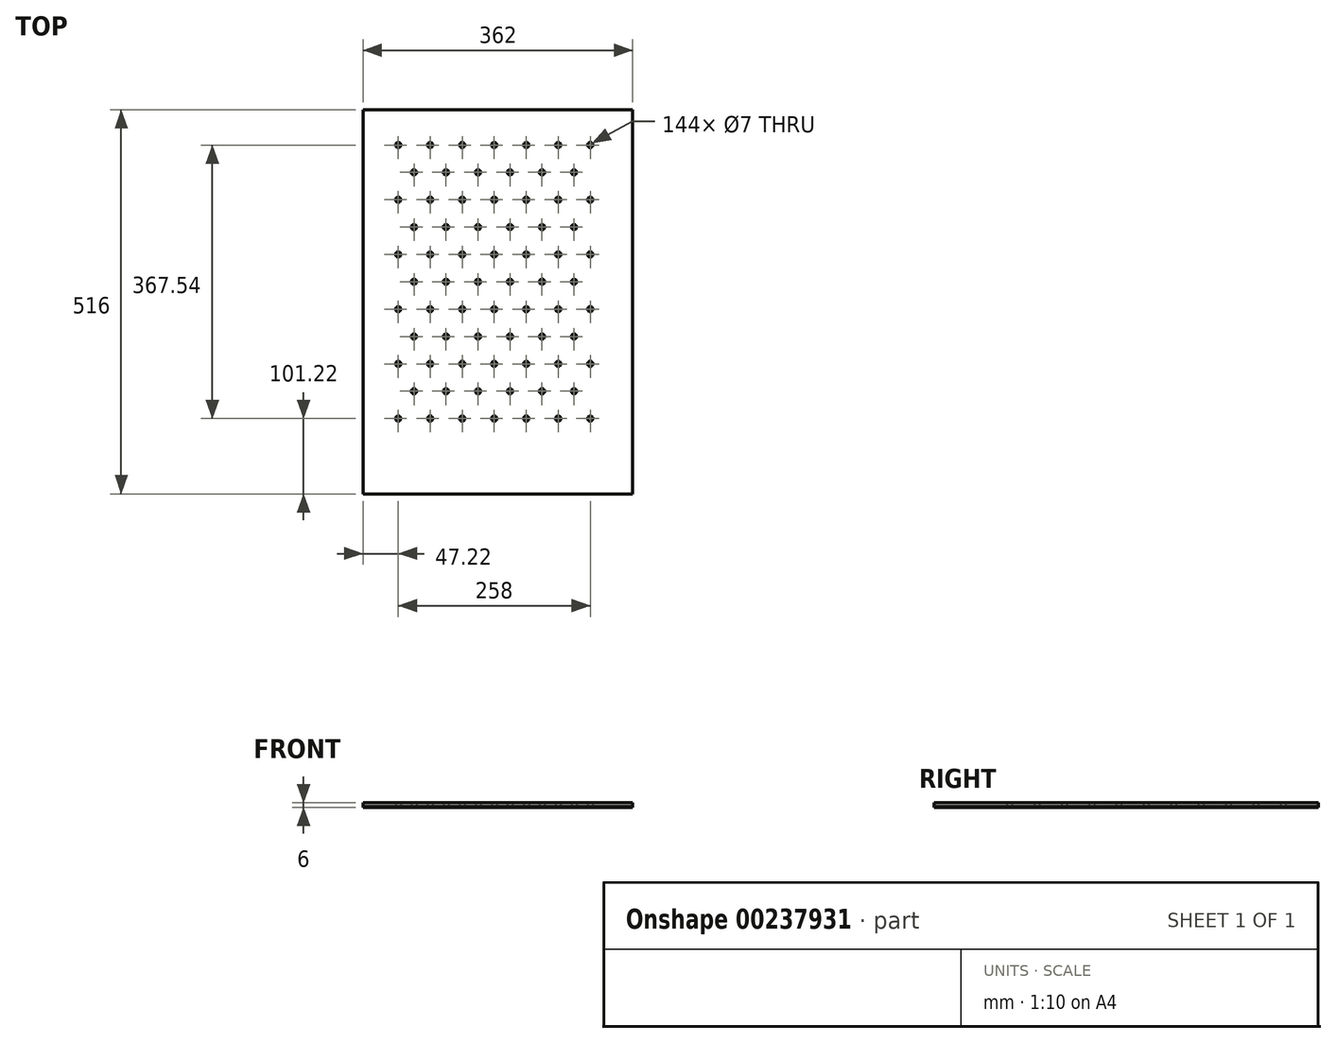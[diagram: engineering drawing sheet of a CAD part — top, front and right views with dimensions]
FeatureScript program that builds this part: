
annotation { "Feature Type Name" : "Feature", "Feature Type Description" : "" }
export const myFeature = defineFeature(function(context is Context, id is Id, definition is map)
    precondition{}
    {
        {
            var Q0;
            Q0=qCreatedBy(makeId("Top.planeOp"),FACE);
            var sketch = newSketch(context, id + "F0", { "sketchPlane" : qUnion([Q0]), "disableImprinting" : false});
            skCircle(sketch, "E0", {"center": v(0, 0) * mm, "radius": 21.22 * mm, "construction": true});
            skLineSegment(sketch, "E1", {"start": v(-21.22, 59.88) * mm, "end": v(-21.22, -39.27) * mm, "construction": true});
            skLineSegment(sketch, "E2", {"start": v(-42.71, -21.22) * mm, "end": v(49.2, -21.22) * mm, "construction": true});
            skLineSegment(sketch, "E3.direction1", {"start": v(0, 0) * mm, "end": v(42.44, 0) * mm, "construction": true});
            skLineSegment(sketch, "E3.direction2", {"start": v(0, -297.48) * mm, "end": v(0, 0) * mm, "construction": true});
            skCircle(sketch, "E4", {"center": v(0, 0) * mm, "radius": 3.5 * mm});
            skCircle(sketch, "E5.0.1.0", {"center": v(0, 73.5) * mm, "radius": 3.5 * mm});
            skCircle(sketch, "E5.0.2.0", {"center": v(0, 147.02) * mm, "radius": 3.5 * mm});
            skCircle(sketch, "E5.0.3.0", {"center": v(0, 220.52) * mm, "radius": 3.5 * mm});
            skCircle(sketch, "E5.0.4.0", {"center": v(0, 294.03) * mm, "radius": 3.5 * mm});
            skCircle(sketch, "E5.0.5.0", {"center": v(0, 367.54) * mm, "radius": 3.5 * mm});
            skCircle(sketch, "E5.1.0.0", {"center": v(43, 0) * mm, "radius": 3.5 * mm});
            skCircle(sketch, "E5.1.1.0", {"center": v(43, 73.5) * mm, "radius": 3.5 * mm});
            skCircle(sketch, "E5.1.2.0", {"center": v(43, 147.02) * mm, "radius": 3.5 * mm});
            skCircle(sketch, "E5.1.3.0", {"center": v(43, 220.52) * mm, "radius": 3.5 * mm});
            skCircle(sketch, "E5.1.4.0", {"center": v(43, 294.03) * mm, "radius": 3.5 * mm});
            skCircle(sketch, "E5.1.5.0", {"center": v(43, 367.54) * mm, "radius": 3.5 * mm});
            skCircle(sketch, "E5.2.0.0", {"center": v(86, 0) * mm, "radius": 3.5 * mm});
            skCircle(sketch, "E5.2.1.0", {"center": v(86, 73.5) * mm, "radius": 3.5 * mm});
            skCircle(sketch, "E5.2.2.0", {"center": v(86, 147.02) * mm, "radius": 3.5 * mm});
            skCircle(sketch, "E5.2.3.0", {"center": v(86, 220.52) * mm, "radius": 3.5 * mm});
            skCircle(sketch, "E5.2.4.0", {"center": v(86, 294.03) * mm, "radius": 3.5 * mm});
            skCircle(sketch, "E5.2.5.0", {"center": v(86, 367.54) * mm, "radius": 3.5 * mm});
            skCircle(sketch, "E5.3.0.0", {"center": v(129, 0) * mm, "radius": 3.5 * mm});
            skCircle(sketch, "E5.3.1.0", {"center": v(129, 73.5) * mm, "radius": 3.5 * mm});
            skCircle(sketch, "E5.3.2.0", {"center": v(129, 147.02) * mm, "radius": 3.5 * mm});
            skCircle(sketch, "E5.3.3.0", {"center": v(129, 220.52) * mm, "radius": 3.5 * mm});
            skCircle(sketch, "E5.3.4.0", {"center": v(129, 294.03) * mm, "radius": 3.5 * mm});
            skCircle(sketch, "E5.3.5.0", {"center": v(129, 367.54) * mm, "radius": 3.5 * mm});
            skCircle(sketch, "E5.4.0.0", {"center": v(172, 0) * mm, "radius": 3.5 * mm});
            skCircle(sketch, "E5.4.1.0", {"center": v(172, 73.5) * mm, "radius": 3.5 * mm});
            skCircle(sketch, "E5.4.2.0", {"center": v(172, 147.02) * mm, "radius": 3.5 * mm});
            skCircle(sketch, "E5.4.3.0", {"center": v(172, 220.52) * mm, "radius": 3.5 * mm});
            skCircle(sketch, "E5.4.4.0", {"center": v(172, 294.03) * mm, "radius": 3.5 * mm});
            skCircle(sketch, "E5.4.5.0", {"center": v(172, 367.54) * mm, "radius": 3.5 * mm});
            skCircle(sketch, "E5.5.0.0", {"center": v(215, 0) * mm, "radius": 3.5 * mm});
            skCircle(sketch, "E5.5.1.0", {"center": v(215, 73.5) * mm, "radius": 3.5 * mm});
            skCircle(sketch, "E5.5.2.0", {"center": v(215, 147.02) * mm, "radius": 3.5 * mm});
            skCircle(sketch, "E5.5.3.0", {"center": v(215, 220.52) * mm, "radius": 3.5 * mm});
            skCircle(sketch, "E5.5.4.0", {"center": v(215, 294.03) * mm, "radius": 3.5 * mm});
            skCircle(sketch, "E5.5.5.0", {"center": v(215, 367.54) * mm, "radius": 3.5 * mm});
            skCircle(sketch, "E5.6.0.0", {"center": v(258, 0) * mm, "radius": 3.5 * mm});
            skCircle(sketch, "E5.6.1.0", {"center": v(258, 73.5) * mm, "radius": 3.5 * mm});
            skCircle(sketch, "E5.6.2.0", {"center": v(258, 147.02) * mm, "radius": 3.5 * mm});
            skCircle(sketch, "E5.6.3.0", {"center": v(258, 220.52) * mm, "radius": 3.5 * mm});
            skCircle(sketch, "E5.6.4.0", {"center": v(258, 294.03) * mm, "radius": 3.5 * mm});
            skCircle(sketch, "E5.6.5.0", {"center": v(258, 367.54) * mm, "radius": 3.5 * mm});
            skLineSegment(sketch, "E5.direction1", {"start": v(0, 0) * mm, "end": v(43, 0) * mm, "construction": true});
            skLineSegment(sketch, "E5.direction2", {"start": v(0, 0) * mm, "end": v(0, 73.5) * mm, "construction": true});
            skLineSegment(sketch, "E6", {"start": v(-21.22, -21.22) * mm, "end": v(288.78, -21.22) * mm, "construction": true});
            skPoint(sketch, "E6.endSnap0", {"position": v(3.24, -21.22) * mm});
            skLineSegment(sketch, "E7", {"start": v(288.78, -21.22) * mm, "end": v(288.78, 388.78) * mm, "construction": true});
            skLineSegment(sketch, "E8", {"start": v(288.78, 388.78) * mm, "end": v(-21.22, 388.78) * mm, "construction": true});
            skLineSegment(sketch, "E9", {"start": v(-21.22, 388.78) * mm, "end": v(-21.22, -21.22) * mm, "construction": true});
            skLineSegment(sketch, "E10", {"start": v(-37.22, 404.78) * mm, "end": v(304.78, 404.78) * mm});
            skLineSegment(sketch, "E11", {"start": v(304.78, 404.78) * mm, "end": v(304.78, -91.22) * mm});
            skLineSegment(sketch, "E12", {"start": v(304.78, -91.22) * mm, "end": v(-37.22, -91.22) * mm});
            skLineSegment(sketch, "E13", {"start": v(-37.22, -91.22) * mm, "end": v(-37.22, 404.78) * mm});
            skCircle(sketch, "E14", {"center": v(42.44, 0) * mm, "radius": 21.22 * mm, "construction": true});
            skCircle(sketch, "E15", {"center": v(21.22, 36.75) * mm, "radius": 21.22 * mm, "construction": true});
            skCircle(sketch, "E16", {"center": v(0, 73.5) * mm, "radius": 21.22 * mm, "construction": true});
            skCircle(sketch, "E17", {"center": v(21.22, 36.75) * mm, "radius": 3.5 * mm});
            skCircle(sketch, "E18.0.1.0", {"center": v(21.22, 110.26) * mm, "radius": 3.5 * mm});
            skCircle(sketch, "E18.0.2.0", {"center": v(21.22, 183.77) * mm, "radius": 3.5 * mm});
            skCircle(sketch, "E18.0.3.0", {"center": v(21.22, 257.28) * mm, "radius": 3.5 * mm});
            skCircle(sketch, "E18.0.4.0", {"center": v(21.22, 330.79) * mm, "radius": 3.5 * mm});
            skCircle(sketch, "E18.1.0.0", {"center": v(64.22, 36.75) * mm, "radius": 3.5 * mm});
            skCircle(sketch, "E18.1.1.0", {"center": v(64.22, 110.26) * mm, "radius": 3.5 * mm});
            skCircle(sketch, "E18.1.2.0", {"center": v(64.22, 183.77) * mm, "radius": 3.5 * mm});
            skCircle(sketch, "E18.1.3.0", {"center": v(64.22, 257.28) * mm, "radius": 3.5 * mm});
            skCircle(sketch, "E18.1.4.0", {"center": v(64.22, 330.79) * mm, "radius": 3.5 * mm});
            skCircle(sketch, "E18.2.0.0", {"center": v(107.22, 36.75) * mm, "radius": 3.5 * mm});
            skCircle(sketch, "E18.2.1.0", {"center": v(107.22, 110.26) * mm, "radius": 3.5 * mm});
            skCircle(sketch, "E18.2.2.0", {"center": v(107.22, 183.77) * mm, "radius": 3.5 * mm});
            skCircle(sketch, "E18.2.3.0", {"center": v(107.22, 257.28) * mm, "radius": 3.5 * mm});
            skCircle(sketch, "E18.2.4.0", {"center": v(107.22, 330.79) * mm, "radius": 3.5 * mm});
            skCircle(sketch, "E18.3.0.0", {"center": v(150.22, 36.75) * mm, "radius": 3.5 * mm});
            skCircle(sketch, "E18.3.1.0", {"center": v(150.22, 110.26) * mm, "radius": 3.5 * mm});
            skCircle(sketch, "E18.3.2.0", {"center": v(150.22, 183.77) * mm, "radius": 3.5 * mm});
            skCircle(sketch, "E18.3.3.0", {"center": v(150.22, 257.28) * mm, "radius": 3.5 * mm});
            skCircle(sketch, "E18.3.4.0", {"center": v(150.22, 330.79) * mm, "radius": 3.5 * mm});
            skCircle(sketch, "E18.4.0.0", {"center": v(193.22, 36.75) * mm, "radius": 3.5 * mm});
            skCircle(sketch, "E18.4.1.0", {"center": v(193.22, 110.26) * mm, "radius": 3.5 * mm});
            skCircle(sketch, "E18.4.2.0", {"center": v(193.22, 183.77) * mm, "radius": 3.5 * mm});
            skCircle(sketch, "E18.4.3.0", {"center": v(193.22, 257.28) * mm, "radius": 3.5 * mm});
            skCircle(sketch, "E18.4.4.0", {"center": v(193.22, 330.79) * mm, "radius": 3.5 * mm});
            skCircle(sketch, "E18.5.0.0", {"center": v(236.22, 36.75) * mm, "radius": 3.5 * mm});
            skCircle(sketch, "E18.5.1.0", {"center": v(236.22, 110.26) * mm, "radius": 3.5 * mm});
            skCircle(sketch, "E18.5.2.0", {"center": v(236.22, 183.77) * mm, "radius": 3.5 * mm});
            skCircle(sketch, "E18.5.3.0", {"center": v(236.22, 257.28) * mm, "radius": 3.5 * mm});
            skCircle(sketch, "E18.5.4.0", {"center": v(236.22, 330.79) * mm, "radius": 3.5 * mm});
            skLineSegment(sketch, "E18.direction1", {"start": v(21.22, 36.75) * mm, "end": v(64.22, 36.75) * mm, "construction": true});
            skLineSegment(sketch, "E18.direction2", {"start": v(21.22, 36.75) * mm, "end": v(21.22, 110.26) * mm, "construction": true});
            skCircle(sketch, "E19", {"center": v(85.72, 171.68) * mm, "radius": 21.17 * mm, "construction": true});
            skLineSegment(sketch, "E20.bottom", {"start": v(80.72, 181.68) * mm, "end": v(90.72, 181.68) * mm, "construction": true});
            skLineSegment(sketch, "E20.top", {"start": v(80.72, 161.68) * mm, "end": v(90.72, 161.68) * mm, "construction": true});
            skLineSegment(sketch, "E20.left", {"start": v(80.72, 181.68) * mm, "end": v(80.72, 161.68) * mm, "construction": true});
            skLineSegment(sketch, "E20.right", {"start": v(90.72, 181.68) * mm, "end": v(90.72, 161.68) * mm, "construction": true});
            skPoint(sketch, "E21.positionSnap0", {"position": v(80.72, 171.68) * mm});
            skPoint(sketch, "E21.positionSnap1", {"position": v(85.72, 181.68) * mm});
            skCircle(sketch, "E22", {"center": v(0, 367.54) * mm, "radius": 21.22 * mm, "construction": true});
            skCircle(sketch, "E23", {"center": v(258, 0) * mm, "radius": 21.22 * mm, "construction": true});
            skSolve(sketch);
        }
        {
            var Q0;
            Q0=makeQuery(id+"F0.imprint","IMPRINT",FACE,{"disambiguationData":[TD([[makeQuery(id+"F0.imprint","IMPRINT",EDGE,{"derivedFrom":sQuery(id+"F0.wireOp",EDGE,"E4")}),-1.0]])]});
            extrude(context, id + "F1", {"entities" : qUnion([Q0]), "depth" : 5 * mm});
        }
        {
            var Q0;
            Q0=makeQuery(id+"F1.opExtrude","CAP_FACE",FACE,{"disambiguationData":[OSD([sQuery(id+"F0.wireOp",EDGE,"E4"),sQuery(id+"F0.wireOp",EDGE,"E5.0.1.0"),sQuery(id+"F0.wireOp",EDGE,"E5.0.2.0"),sQuery(id+"F0.wireOp",EDGE,"E5.0.3.0"),sQuery(id+"F0.wireOp",EDGE,"E5.0.4.0"),sQuery(id+"F0.wireOp",EDGE,"E5.0.5.0"),sQuery(id+"F0.wireOp",EDGE,"E5.1.0.0"),sQuery(id+"F0.wireOp",EDGE,"E5.1.1.0"),sQuery(id+"F0.wireOp",EDGE,"E5.1.2.0"),sQuery(id+"F0.wireOp",EDGE,"E5.1.3.0"),sQuery(id+"F0.wireOp",EDGE,"E5.1.4.0"),sQuery(id+"F0.wireOp",EDGE,"E5.1.5.0"),sQuery(id+"F0.wireOp",EDGE,"E5.2.0.0"),sQuery(id+"F0.wireOp",EDGE,"E5.2.1.0"),sQuery(id+"F0.wireOp",EDGE,"E5.2.2.0"),sQuery(id+"F0.wireOp",EDGE,"E5.2.3.0"),sQuery(id+"F0.wireOp",EDGE,"E5.2.4.0"),sQuery(id+"F0.wireOp",EDGE,"E5.2.5.0"),sQuery(id+"F0.wireOp",EDGE,"E5.3.0.0"),sQuery(id+"F0.wireOp",EDGE,"E5.3.1.0"),sQuery(id+"F0.wireOp",EDGE,"E5.3.2.0"),sQuery(id+"F0.wireOp",EDGE,"E5.3.3.0"),sQuery(id+"F0.wireOp",EDGE,"E5.3.4.0"),sQuery(id+"F0.wireOp",EDGE,"E5.3.5.0"),sQuery(id+"F0.wireOp",EDGE,"E5.4.0.0"),sQuery(id+"F0.wireOp",EDGE,"E5.4.1.0"),sQuery(id+"F0.wireOp",EDGE,"E5.4.2.0"),sQuery(id+"F0.wireOp",EDGE,"E5.4.3.0"),sQuery(id+"F0.wireOp",EDGE,"E5.4.4.0"),sQuery(id+"F0.wireOp",EDGE,"E5.4.5.0"),sQuery(id+"F0.wireOp",EDGE,"E5.5.0.0"),sQuery(id+"F0.wireOp",EDGE,"E5.5.1.0"),sQuery(id+"F0.wireOp",EDGE,"E5.5.2.0"),sQuery(id+"F0.wireOp",EDGE,"E5.5.3.0"),sQuery(id+"F0.wireOp",EDGE,"E5.5.4.0"),sQuery(id+"F0.wireOp",EDGE,"E5.5.5.0"),sQuery(id+"F0.wireOp",EDGE,"E5.6.0.0"),sQuery(id+"F0.wireOp",EDGE,"E5.6.1.0"),sQuery(id+"F0.wireOp",EDGE,"E5.6.2.0"),sQuery(id+"F0.wireOp",EDGE,"E5.6.3.0"),sQuery(id+"F0.wireOp",EDGE,"E5.6.4.0"),sQuery(id+"F0.wireOp",EDGE,"E5.6.5.0"),sQuery(id+"F0.wireOp",EDGE,"b43360bd-87d0-4ba4-b8e7-1d9b1ca2d7b7.0.7.0"),sQuery(id+"F0.wireOp",EDGE,"b43360bd-87d0-4ba4-b8e7-1d9b1ca2d7b7.0.7.1"),sQuery(id+"F0.wireOp",EDGE,"b43360bd-87d0-4ba4-b8e7-1d9b1ca2d7b7.0.7.2"),sQuery(id+"F0.wireOp",EDGE,"b43360bd-87d0-4ba4-b8e7-1d9b1ca2d7b7.0.7.3"),sQuery(id+"F0.wireOp",EDGE,"b43360bd-87d0-4ba4-b8e7-1d9b1ca2d7b7.0.7.4"),sQuery(id+"F0.wireOp",EDGE,"b43360bd-87d0-4ba4-b8e7-1d9b1ca2d7b7.0.7.5"),sQuery(id+"F0.wireOp",EDGE,"b43360bd-87d0-4ba4-b8e7-1d9b1ca2d7b7.0.8.0"),sQuery(id+"F0.wireOp",EDGE,"b43360bd-87d0-4ba4-b8e7-1d9b1ca2d7b7.0.8.1"),sQuery(id+"F0.wireOp",EDGE,"b43360bd-87d0-4ba4-b8e7-1d9b1ca2d7b7.0.8.2"),sQuery(id+"F0.wireOp",EDGE,"b43360bd-87d0-4ba4-b8e7-1d9b1ca2d7b7.0.8.3"),sQuery(id+"F0.wireOp",EDGE,"b43360bd-87d0-4ba4-b8e7-1d9b1ca2d7b7.0.8.4"),sQuery(id+"F0.wireOp",EDGE,"b43360bd-87d0-4ba4-b8e7-1d9b1ca2d7b7.0.8.5"),sQuery(id+"F0.wireOp",EDGE,"4d49d44f-d1c3-4a0c-bbbb-6a01bf94c153.0.9.0"),sQuery(id+"F0.wireOp",EDGE,"4d49d44f-d1c3-4a0c-bbbb-6a01bf94c153.0.9.1"),sQuery(id+"F0.wireOp",EDGE,"4d49d44f-d1c3-4a0c-bbbb-6a01bf94c153.0.9.2"),sQuery(id+"F0.wireOp",EDGE,"4d49d44f-d1c3-4a0c-bbbb-6a01bf94c153.0.9.3"),sQuery(id+"F0.wireOp",EDGE,"4d49d44f-d1c3-4a0c-bbbb-6a01bf94c153.0.9.4"),sQuery(id+"F0.wireOp",EDGE,"4d49d44f-d1c3-4a0c-bbbb-6a01bf94c153.0.9.5"),sQuery(id+"F0.wireOp",EDGE,"E10"),sQuery(id+"F0.wireOp",EDGE,"E11"),sQuery(id+"F0.wireOp",EDGE,"E12"),sQuery(id+"F0.wireOp",EDGE,"E13"),sQuery(id+"F0.wireOp",EDGE,"ce14f02e-7be2-4b20-84b1-1cf9d0b90355.0.0.6"),sQuery(id+"F0.wireOp",EDGE,"ce14f02e-7be2-4b20-84b1-1cf9d0b90355.0.0.7"),sQuery(id+"F0.wireOp",EDGE,"ce14f02e-7be2-4b20-84b1-1cf9d0b90355.0.1.6"),sQuery(id+"F0.wireOp",EDGE,"ce14f02e-7be2-4b20-84b1-1cf9d0b90355.0.1.7"),sQuery(id+"F0.wireOp",EDGE,"ce14f02e-7be2-4b20-84b1-1cf9d0b90355.0.2.6"),sQuery(id+"F0.wireOp",EDGE,"ce14f02e-7be2-4b20-84b1-1cf9d0b90355.0.2.7"),sQuery(id+"F0.wireOp",EDGE,"ce14f02e-7be2-4b20-84b1-1cf9d0b90355.0.3.6"),sQuery(id+"F0.wireOp",EDGE,"ce14f02e-7be2-4b20-84b1-1cf9d0b90355.0.3.7"),sQuery(id+"F0.wireOp",EDGE,"ce14f02e-7be2-4b20-84b1-1cf9d0b90355.0.4.6"),sQuery(id+"F0.wireOp",EDGE,"ce14f02e-7be2-4b20-84b1-1cf9d0b90355.0.4.7"),sQuery(id+"F0.wireOp",EDGE,"ce14f02e-7be2-4b20-84b1-1cf9d0b90355.0.5.6"),sQuery(id+"F0.wireOp",EDGE,"ce14f02e-7be2-4b20-84b1-1cf9d0b90355.0.5.7"),sQuery(id+"F0.wireOp",EDGE,"ce14f02e-7be2-4b20-84b1-1cf9d0b90355.0.6.6"),sQuery(id+"F0.wireOp",EDGE,"ce14f02e-7be2-4b20-84b1-1cf9d0b90355.0.6.7"),sQuery(id+"F0.wireOp",EDGE,"ce14f02e-7be2-4b20-84b1-1cf9d0b90355.0.7.6"),sQuery(id+"F0.wireOp",EDGE,"ce14f02e-7be2-4b20-84b1-1cf9d0b90355.0.7.7"),sQuery(id+"F0.wireOp",EDGE,"ce14f02e-7be2-4b20-84b1-1cf9d0b90355.0.8.6"),sQuery(id+"F0.wireOp",EDGE,"ce14f02e-7be2-4b20-84b1-1cf9d0b90355.0.8.7"),sQuery(id+"F0.wireOp",EDGE,"ce14f02e-7be2-4b20-84b1-1cf9d0b90355.0.9.6"),sQuery(id+"F0.wireOp",EDGE,"ce14f02e-7be2-4b20-84b1-1cf9d0b90355.0.9.7"),sQuery(id+"F0.wireOp",EDGE,"E17"),sQuery(id+"F0.wireOp",EDGE,"E18.0.1.0"),sQuery(id+"F0.wireOp",EDGE,"E18.0.2.0"),sQuery(id+"F0.wireOp",EDGE,"E18.0.3.0"),sQuery(id+"F0.wireOp",EDGE,"E18.0.4.0"),sQuery(id+"F0.wireOp",EDGE,"E18.0.5.0"),sQuery(id+"F0.wireOp",EDGE,"E18.0.6.0"),sQuery(id+"F0.wireOp",EDGE,"E18.1.0.0"),sQuery(id+"F0.wireOp",EDGE,"E18.1.1.0"),sQuery(id+"F0.wireOp",EDGE,"E18.1.2.0"),sQuery(id+"F0.wireOp",EDGE,"E18.1.3.0"),sQuery(id+"F0.wireOp",EDGE,"E18.1.4.0"),sQuery(id+"F0.wireOp",EDGE,"E18.1.5.0"),sQuery(id+"F0.wireOp",EDGE,"E18.1.6.0"),sQuery(id+"F0.wireOp",EDGE,"E18.2.0.0"),sQuery(id+"F0.wireOp",EDGE,"E18.2.1.0"),sQuery(id+"F0.wireOp",EDGE,"E18.2.2.0"),sQuery(id+"F0.wireOp",EDGE,"E18.2.3.0"),sQuery(id+"F0.wireOp",EDGE,"E18.2.4.0"),sQuery(id+"F0.wireOp",EDGE,"E18.2.5.0"),sQuery(id+"F0.wireOp",EDGE,"E18.2.6.0"),sQuery(id+"F0.wireOp",EDGE,"E18.3.0.0"),sQuery(id+"F0.wireOp",EDGE,"E18.3.1.0"),sQuery(id+"F0.wireOp",EDGE,"E18.3.2.0"),sQuery(id+"F0.wireOp",EDGE,"E18.3.3.0"),sQuery(id+"F0.wireOp",EDGE,"E18.3.4.0"),sQuery(id+"F0.wireOp",EDGE,"E18.3.5.0"),sQuery(id+"F0.wireOp",EDGE,"E18.3.6.0"),sQuery(id+"F0.wireOp",EDGE,"E18.4.0.0"),sQuery(id+"F0.wireOp",EDGE,"E18.4.1.0"),sQuery(id+"F0.wireOp",EDGE,"E18.4.2.0"),sQuery(id+"F0.wireOp",EDGE,"E18.4.3.0"),sQuery(id+"F0.wireOp",EDGE,"E18.4.4.0"),sQuery(id+"F0.wireOp",EDGE,"E18.4.5.0"),sQuery(id+"F0.wireOp",EDGE,"E18.4.6.0"),sQuery(id+"F0.wireOp",EDGE,"E18.5.0.0"),sQuery(id+"F0.wireOp",EDGE,"E18.5.1.0"),sQuery(id+"F0.wireOp",EDGE,"E18.5.2.0"),sQuery(id+"F0.wireOp",EDGE,"E18.5.3.0"),sQuery(id+"F0.wireOp",EDGE,"E18.5.4.0"),sQuery(id+"F0.wireOp",EDGE,"E18.5.5.0"),sQuery(id+"F0.wireOp",EDGE,"E18.5.6.0"),sQuery(id+"F0.wireOp",EDGE,"E18.6.0.0"),sQuery(id+"F0.wireOp",EDGE,"E18.6.1.0"),sQuery(id+"F0.wireOp",EDGE,"E18.6.2.0"),sQuery(id+"F0.wireOp",EDGE,"E18.6.3.0"),sQuery(id+"F0.wireOp",EDGE,"E18.6.4.0"),sQuery(id+"F0.wireOp",EDGE,"E18.6.5.0"),sQuery(id+"F0.wireOp",EDGE,"E18.6.6.0"),sQuery(id+"F0.wireOp",EDGE,"E18.7.0.0"),sQuery(id+"F0.wireOp",EDGE,"E18.7.1.0"),sQuery(id+"F0.wireOp",EDGE,"E18.7.2.0"),sQuery(id+"F0.wireOp",EDGE,"E18.7.3.0"),sQuery(id+"F0.wireOp",EDGE,"E18.7.4.0"),sQuery(id+"F0.wireOp",EDGE,"E18.7.5.0"),sQuery(id+"F0.wireOp",EDGE,"E18.7.6.0"),sQuery(id+"F0.wireOp",EDGE,"E18.8.0.0"),sQuery(id+"F0.wireOp",EDGE,"E18.8.1.0"),sQuery(id+"F0.wireOp",EDGE,"E18.8.2.0"),sQuery(id+"F0.wireOp",EDGE,"E18.8.3.0"),sQuery(id+"F0.wireOp",EDGE,"E18.8.4.0"),sQuery(id+"F0.wireOp",EDGE,"E18.8.5.0"),sQuery(id+"F0.wireOp",EDGE,"E18.8.6.0"),sQuery(id+"F0.wireOp",EDGE,"E18.9.0.0"),sQuery(id+"F0.wireOp",EDGE,"E18.9.1.0"),sQuery(id+"F0.wireOp",EDGE,"E18.9.2.0"),sQuery(id+"F0.wireOp",EDGE,"E18.9.3.0"),sQuery(id+"F0.wireOp",EDGE,"E18.9.4.0"),sQuery(id+"F0.wireOp",EDGE,"E18.9.5.0"),sQuery(id+"F0.wireOp",EDGE,"E18.9.6.0"),sQuery(id+"F0.wireOp",EDGE,"0ecf2793-63ef-4b24-9386-6ba147f8df1b.0.0.7"),sQuery(id+"F0.wireOp",EDGE,"0ecf2793-63ef-4b24-9386-6ba147f8df1b.0.1.7"),sQuery(id+"F0.wireOp",EDGE,"0ecf2793-63ef-4b24-9386-6ba147f8df1b.0.2.7"),sQuery(id+"F0.wireOp",EDGE,"0ecf2793-63ef-4b24-9386-6ba147f8df1b.0.3.7"),sQuery(id+"F0.wireOp",EDGE,"0ecf2793-63ef-4b24-9386-6ba147f8df1b.0.4.7"),sQuery(id+"F0.wireOp",EDGE,"0ecf2793-63ef-4b24-9386-6ba147f8df1b.0.5.7"),sQuery(id+"F0.wireOp",EDGE,"0ecf2793-63ef-4b24-9386-6ba147f8df1b.0.6.7"),sQuery(id+"F0.wireOp",EDGE,"0ecf2793-63ef-4b24-9386-6ba147f8df1b.0.7.7"),sQuery(id+"F0.wireOp",EDGE,"0ecf2793-63ef-4b24-9386-6ba147f8df1b.0.8.7"),sQuery(id+"F0.wireOp",EDGE,"0ecf2793-63ef-4b24-9386-6ba147f8df1b.0.9.7")])],"isStart":true});
            var sketch = newSketch(context, id + "F2", { "sketchPlane" : qUnion([Q0]), "disableImprinting" : false});
            skLineSegment(sketch, "E24", {"start": v(13.78, 71.22) * mm, "end": v(-37.22, 71.22) * mm, "construction": true});
            skLineSegment(sketch, "E25", {"start": v(253.78, 71.22) * mm, "end": v(304.78, 71.22) * mm, "construction": true});
            skSolve(sketch);
        }
        {
            var Q0;
            Q0=makeQuery(id+"F1.opExtrude","CAP_FACE",FACE,{"disambiguationData":[OSD([sQuery(id+"F0.wireOp",EDGE,"E4"),sQuery(id+"F0.wireOp",EDGE,"E5.0.1.0"),sQuery(id+"F0.wireOp",EDGE,"E5.0.2.0"),sQuery(id+"F0.wireOp",EDGE,"E5.0.3.0"),sQuery(id+"F0.wireOp",EDGE,"E5.0.4.0"),sQuery(id+"F0.wireOp",EDGE,"E5.0.5.0"),sQuery(id+"F0.wireOp",EDGE,"E5.1.0.0"),sQuery(id+"F0.wireOp",EDGE,"E5.1.1.0"),sQuery(id+"F0.wireOp",EDGE,"E5.1.2.0"),sQuery(id+"F0.wireOp",EDGE,"E5.1.3.0"),sQuery(id+"F0.wireOp",EDGE,"E5.1.4.0"),sQuery(id+"F0.wireOp",EDGE,"E5.1.5.0"),sQuery(id+"F0.wireOp",EDGE,"E5.2.0.0"),sQuery(id+"F0.wireOp",EDGE,"E5.2.1.0"),sQuery(id+"F0.wireOp",EDGE,"E5.2.2.0"),sQuery(id+"F0.wireOp",EDGE,"E5.2.3.0"),sQuery(id+"F0.wireOp",EDGE,"E5.2.4.0"),sQuery(id+"F0.wireOp",EDGE,"E5.2.5.0"),sQuery(id+"F0.wireOp",EDGE,"E5.3.0.0"),sQuery(id+"F0.wireOp",EDGE,"E5.3.1.0"),sQuery(id+"F0.wireOp",EDGE,"E5.3.2.0"),sQuery(id+"F0.wireOp",EDGE,"E5.3.3.0"),sQuery(id+"F0.wireOp",EDGE,"E5.3.4.0"),sQuery(id+"F0.wireOp",EDGE,"E5.3.5.0"),sQuery(id+"F0.wireOp",EDGE,"E5.4.0.0"),sQuery(id+"F0.wireOp",EDGE,"E5.4.1.0"),sQuery(id+"F0.wireOp",EDGE,"E5.4.2.0"),sQuery(id+"F0.wireOp",EDGE,"E5.4.3.0"),sQuery(id+"F0.wireOp",EDGE,"E5.4.4.0"),sQuery(id+"F0.wireOp",EDGE,"E5.4.5.0"),sQuery(id+"F0.wireOp",EDGE,"E5.5.0.0"),sQuery(id+"F0.wireOp",EDGE,"E5.5.1.0"),sQuery(id+"F0.wireOp",EDGE,"E5.5.2.0"),sQuery(id+"F0.wireOp",EDGE,"E5.5.3.0"),sQuery(id+"F0.wireOp",EDGE,"E5.5.4.0"),sQuery(id+"F0.wireOp",EDGE,"E5.5.5.0"),sQuery(id+"F0.wireOp",EDGE,"E5.6.0.0"),sQuery(id+"F0.wireOp",EDGE,"E5.6.1.0"),sQuery(id+"F0.wireOp",EDGE,"E5.6.2.0"),sQuery(id+"F0.wireOp",EDGE,"E5.6.3.0"),sQuery(id+"F0.wireOp",EDGE,"E5.6.4.0"),sQuery(id+"F0.wireOp",EDGE,"E5.6.5.0"),sQuery(id+"F0.wireOp",EDGE,"b43360bd-87d0-4ba4-b8e7-1d9b1ca2d7b7.0.7.0"),sQuery(id+"F0.wireOp",EDGE,"b43360bd-87d0-4ba4-b8e7-1d9b1ca2d7b7.0.7.1"),sQuery(id+"F0.wireOp",EDGE,"b43360bd-87d0-4ba4-b8e7-1d9b1ca2d7b7.0.7.2"),sQuery(id+"F0.wireOp",EDGE,"b43360bd-87d0-4ba4-b8e7-1d9b1ca2d7b7.0.7.3"),sQuery(id+"F0.wireOp",EDGE,"b43360bd-87d0-4ba4-b8e7-1d9b1ca2d7b7.0.7.4"),sQuery(id+"F0.wireOp",EDGE,"b43360bd-87d0-4ba4-b8e7-1d9b1ca2d7b7.0.7.5"),sQuery(id+"F0.wireOp",EDGE,"b43360bd-87d0-4ba4-b8e7-1d9b1ca2d7b7.0.8.0"),sQuery(id+"F0.wireOp",EDGE,"b43360bd-87d0-4ba4-b8e7-1d9b1ca2d7b7.0.8.1"),sQuery(id+"F0.wireOp",EDGE,"b43360bd-87d0-4ba4-b8e7-1d9b1ca2d7b7.0.8.2"),sQuery(id+"F0.wireOp",EDGE,"b43360bd-87d0-4ba4-b8e7-1d9b1ca2d7b7.0.8.3"),sQuery(id+"F0.wireOp",EDGE,"b43360bd-87d0-4ba4-b8e7-1d9b1ca2d7b7.0.8.4"),sQuery(id+"F0.wireOp",EDGE,"b43360bd-87d0-4ba4-b8e7-1d9b1ca2d7b7.0.8.5"),sQuery(id+"F0.wireOp",EDGE,"4d49d44f-d1c3-4a0c-bbbb-6a01bf94c153.0.9.0"),sQuery(id+"F0.wireOp",EDGE,"4d49d44f-d1c3-4a0c-bbbb-6a01bf94c153.0.9.1"),sQuery(id+"F0.wireOp",EDGE,"4d49d44f-d1c3-4a0c-bbbb-6a01bf94c153.0.9.2"),sQuery(id+"F0.wireOp",EDGE,"4d49d44f-d1c3-4a0c-bbbb-6a01bf94c153.0.9.3"),sQuery(id+"F0.wireOp",EDGE,"4d49d44f-d1c3-4a0c-bbbb-6a01bf94c153.0.9.4"),sQuery(id+"F0.wireOp",EDGE,"4d49d44f-d1c3-4a0c-bbbb-6a01bf94c153.0.9.5"),sQuery(id+"F0.wireOp",EDGE,"E10"),sQuery(id+"F0.wireOp",EDGE,"E11"),sQuery(id+"F0.wireOp",EDGE,"E12"),sQuery(id+"F0.wireOp",EDGE,"E13"),sQuery(id+"F0.wireOp",EDGE,"ce14f02e-7be2-4b20-84b1-1cf9d0b90355.0.0.6"),sQuery(id+"F0.wireOp",EDGE,"ce14f02e-7be2-4b20-84b1-1cf9d0b90355.0.0.7"),sQuery(id+"F0.wireOp",EDGE,"ce14f02e-7be2-4b20-84b1-1cf9d0b90355.0.1.6"),sQuery(id+"F0.wireOp",EDGE,"ce14f02e-7be2-4b20-84b1-1cf9d0b90355.0.1.7"),sQuery(id+"F0.wireOp",EDGE,"ce14f02e-7be2-4b20-84b1-1cf9d0b90355.0.2.6"),sQuery(id+"F0.wireOp",EDGE,"ce14f02e-7be2-4b20-84b1-1cf9d0b90355.0.2.7"),sQuery(id+"F0.wireOp",EDGE,"ce14f02e-7be2-4b20-84b1-1cf9d0b90355.0.3.6"),sQuery(id+"F0.wireOp",EDGE,"ce14f02e-7be2-4b20-84b1-1cf9d0b90355.0.3.7"),sQuery(id+"F0.wireOp",EDGE,"ce14f02e-7be2-4b20-84b1-1cf9d0b90355.0.4.6"),sQuery(id+"F0.wireOp",EDGE,"ce14f02e-7be2-4b20-84b1-1cf9d0b90355.0.4.7"),sQuery(id+"F0.wireOp",EDGE,"ce14f02e-7be2-4b20-84b1-1cf9d0b90355.0.5.6"),sQuery(id+"F0.wireOp",EDGE,"ce14f02e-7be2-4b20-84b1-1cf9d0b90355.0.5.7"),sQuery(id+"F0.wireOp",EDGE,"ce14f02e-7be2-4b20-84b1-1cf9d0b90355.0.6.6"),sQuery(id+"F0.wireOp",EDGE,"ce14f02e-7be2-4b20-84b1-1cf9d0b90355.0.6.7"),sQuery(id+"F0.wireOp",EDGE,"ce14f02e-7be2-4b20-84b1-1cf9d0b90355.0.7.6"),sQuery(id+"F0.wireOp",EDGE,"ce14f02e-7be2-4b20-84b1-1cf9d0b90355.0.7.7"),sQuery(id+"F0.wireOp",EDGE,"ce14f02e-7be2-4b20-84b1-1cf9d0b90355.0.8.6"),sQuery(id+"F0.wireOp",EDGE,"ce14f02e-7be2-4b20-84b1-1cf9d0b90355.0.8.7"),sQuery(id+"F0.wireOp",EDGE,"ce14f02e-7be2-4b20-84b1-1cf9d0b90355.0.9.6"),sQuery(id+"F0.wireOp",EDGE,"ce14f02e-7be2-4b20-84b1-1cf9d0b90355.0.9.7"),sQuery(id+"F0.wireOp",EDGE,"E17"),sQuery(id+"F0.wireOp",EDGE,"E18.0.1.0"),sQuery(id+"F0.wireOp",EDGE,"E18.0.2.0"),sQuery(id+"F0.wireOp",EDGE,"E18.0.3.0"),sQuery(id+"F0.wireOp",EDGE,"E18.0.4.0"),sQuery(id+"F0.wireOp",EDGE,"E18.0.5.0"),sQuery(id+"F0.wireOp",EDGE,"E18.0.6.0"),sQuery(id+"F0.wireOp",EDGE,"E18.1.0.0"),sQuery(id+"F0.wireOp",EDGE,"E18.1.1.0"),sQuery(id+"F0.wireOp",EDGE,"E18.1.2.0"),sQuery(id+"F0.wireOp",EDGE,"E18.1.3.0"),sQuery(id+"F0.wireOp",EDGE,"E18.1.4.0"),sQuery(id+"F0.wireOp",EDGE,"E18.1.5.0"),sQuery(id+"F0.wireOp",EDGE,"E18.1.6.0"),sQuery(id+"F0.wireOp",EDGE,"E18.2.0.0"),sQuery(id+"F0.wireOp",EDGE,"E18.2.1.0"),sQuery(id+"F0.wireOp",EDGE,"E18.2.2.0"),sQuery(id+"F0.wireOp",EDGE,"E18.2.3.0"),sQuery(id+"F0.wireOp",EDGE,"E18.2.4.0"),sQuery(id+"F0.wireOp",EDGE,"E18.2.5.0"),sQuery(id+"F0.wireOp",EDGE,"E18.2.6.0"),sQuery(id+"F0.wireOp",EDGE,"E18.3.0.0"),sQuery(id+"F0.wireOp",EDGE,"E18.3.1.0"),sQuery(id+"F0.wireOp",EDGE,"E18.3.2.0"),sQuery(id+"F0.wireOp",EDGE,"E18.3.3.0"),sQuery(id+"F0.wireOp",EDGE,"E18.3.4.0"),sQuery(id+"F0.wireOp",EDGE,"E18.3.5.0"),sQuery(id+"F0.wireOp",EDGE,"E18.3.6.0"),sQuery(id+"F0.wireOp",EDGE,"E18.4.0.0"),sQuery(id+"F0.wireOp",EDGE,"E18.4.1.0"),sQuery(id+"F0.wireOp",EDGE,"E18.4.2.0"),sQuery(id+"F0.wireOp",EDGE,"E18.4.3.0"),sQuery(id+"F0.wireOp",EDGE,"E18.4.4.0"),sQuery(id+"F0.wireOp",EDGE,"E18.4.5.0"),sQuery(id+"F0.wireOp",EDGE,"E18.4.6.0"),sQuery(id+"F0.wireOp",EDGE,"E18.5.0.0"),sQuery(id+"F0.wireOp",EDGE,"E18.5.1.0"),sQuery(id+"F0.wireOp",EDGE,"E18.5.2.0"),sQuery(id+"F0.wireOp",EDGE,"E18.5.3.0"),sQuery(id+"F0.wireOp",EDGE,"E18.5.4.0"),sQuery(id+"F0.wireOp",EDGE,"E18.5.5.0"),sQuery(id+"F0.wireOp",EDGE,"E18.5.6.0"),sQuery(id+"F0.wireOp",EDGE,"E18.6.0.0"),sQuery(id+"F0.wireOp",EDGE,"E18.6.1.0"),sQuery(id+"F0.wireOp",EDGE,"E18.6.2.0"),sQuery(id+"F0.wireOp",EDGE,"E18.6.3.0"),sQuery(id+"F0.wireOp",EDGE,"E18.6.4.0"),sQuery(id+"F0.wireOp",EDGE,"E18.6.5.0"),sQuery(id+"F0.wireOp",EDGE,"E18.6.6.0"),sQuery(id+"F0.wireOp",EDGE,"E18.7.0.0"),sQuery(id+"F0.wireOp",EDGE,"E18.7.1.0"),sQuery(id+"F0.wireOp",EDGE,"E18.7.2.0"),sQuery(id+"F0.wireOp",EDGE,"E18.7.3.0"),sQuery(id+"F0.wireOp",EDGE,"E18.7.4.0"),sQuery(id+"F0.wireOp",EDGE,"E18.7.5.0"),sQuery(id+"F0.wireOp",EDGE,"E18.7.6.0"),sQuery(id+"F0.wireOp",EDGE,"E18.8.0.0"),sQuery(id+"F0.wireOp",EDGE,"E18.8.1.0"),sQuery(id+"F0.wireOp",EDGE,"E18.8.2.0"),sQuery(id+"F0.wireOp",EDGE,"E18.8.3.0"),sQuery(id+"F0.wireOp",EDGE,"E18.8.4.0"),sQuery(id+"F0.wireOp",EDGE,"E18.8.5.0"),sQuery(id+"F0.wireOp",EDGE,"E18.8.6.0"),sQuery(id+"F0.wireOp",EDGE,"E18.9.0.0"),sQuery(id+"F0.wireOp",EDGE,"E18.9.1.0"),sQuery(id+"F0.wireOp",EDGE,"E18.9.2.0"),sQuery(id+"F0.wireOp",EDGE,"E18.9.3.0"),sQuery(id+"F0.wireOp",EDGE,"E18.9.4.0"),sQuery(id+"F0.wireOp",EDGE,"E18.9.5.0"),sQuery(id+"F0.wireOp",EDGE,"E18.9.6.0"),sQuery(id+"F0.wireOp",EDGE,"0ecf2793-63ef-4b24-9386-6ba147f8df1b.0.0.7"),sQuery(id+"F0.wireOp",EDGE,"0ecf2793-63ef-4b24-9386-6ba147f8df1b.0.1.7"),sQuery(id+"F0.wireOp",EDGE,"0ecf2793-63ef-4b24-9386-6ba147f8df1b.0.2.7"),sQuery(id+"F0.wireOp",EDGE,"0ecf2793-63ef-4b24-9386-6ba147f8df1b.0.3.7"),sQuery(id+"F0.wireOp",EDGE,"0ecf2793-63ef-4b24-9386-6ba147f8df1b.0.4.7"),sQuery(id+"F0.wireOp",EDGE,"0ecf2793-63ef-4b24-9386-6ba147f8df1b.0.5.7"),sQuery(id+"F0.wireOp",EDGE,"0ecf2793-63ef-4b24-9386-6ba147f8df1b.0.6.7"),sQuery(id+"F0.wireOp",EDGE,"0ecf2793-63ef-4b24-9386-6ba147f8df1b.0.7.7"),sQuery(id+"F0.wireOp",EDGE,"0ecf2793-63ef-4b24-9386-6ba147f8df1b.0.8.7"),sQuery(id+"F0.wireOp",EDGE,"0ecf2793-63ef-4b24-9386-6ba147f8df1b.0.9.7")])],"isStart":true});
            var sketch = newSketch(context, id + "F3", { "sketchPlane" : qUnion([Q0])});
            skLineSegment(sketch, "E26.0", {"start": v(314.78, -414.78) * mm, "end": v(314.78, 101.22) * mm});
            skLineSegment(sketch, "E26.1", {"start": v(-47.22, -414.78) * mm, "end": v(314.78, -414.78) * mm});
            skLineSegment(sketch, "E26.2", {"start": v(-47.22, 101.22) * mm, "end": v(-47.22, -414.78) * mm});
            skLineSegment(sketch, "E26.3", {"start": v(314.78, 101.22) * mm, "end": v(-47.22, 101.22) * mm});
            skSolve(sketch);
        }
        {
            var Q0;
            Q0=makeQuery(id+"F3.imprint","IMPRINT",FACE,{"disambiguationData":[TD([[makeQuery(id+"F3.imprint","IMPRINT",EDGE,{"derivedFrom":sQuery(id+"F3.wireOp",EDGE,"E26.0")}),1.0]])]});
            extrude(context, id + "F4", {"entities" : qUnion([Q0]), "operationType" : NewBodyOperationType.ADD, "oppositeDirection" : true, "depth" : 5 * mm});
        }
        {
            var Q0;
            {var subQ0=sQuery(id+"F0.wireOp",EDGE,"E13");var subQ1=sQuery(id+"F0.wireOp",EDGE,"E12");var subQ2=sQuery(id+"F0.wireOp",EDGE,"E11");var subQ3=sQuery(id+"F0.wireOp",EDGE,"E10");Q0=makeQuery(id+"F4.boolean.opBoolean","MERGE",FACE,{"derivedFrom":[makeQuery(id+"F1.opExtrude","CAP_FACE",FACE,{"disambiguationData":[OSD([sQuery(id+"F0.wireOp",EDGE,"E4"),sQuery(id+"F0.wireOp",EDGE,"E5.0.1.0"),sQuery(id+"F0.wireOp",EDGE,"E5.0.2.0"),sQuery(id+"F0.wireOp",EDGE,"E5.0.3.0"),sQuery(id+"F0.wireOp",EDGE,"E5.0.4.0"),sQuery(id+"F0.wireOp",EDGE,"E5.0.5.0"),sQuery(id+"F0.wireOp",EDGE,"E5.1.0.0"),sQuery(id+"F0.wireOp",EDGE,"E5.1.1.0"),sQuery(id+"F0.wireOp",EDGE,"E5.1.2.0"),sQuery(id+"F0.wireOp",EDGE,"E5.1.3.0"),sQuery(id+"F0.wireOp",EDGE,"E5.1.4.0"),sQuery(id+"F0.wireOp",EDGE,"E5.1.5.0"),sQuery(id+"F0.wireOp",EDGE,"E5.2.0.0"),sQuery(id+"F0.wireOp",EDGE,"E5.2.1.0"),sQuery(id+"F0.wireOp",EDGE,"E5.2.2.0"),sQuery(id+"F0.wireOp",EDGE,"E5.2.3.0"),sQuery(id+"F0.wireOp",EDGE,"E5.2.4.0"),sQuery(id+"F0.wireOp",EDGE,"E5.2.5.0"),sQuery(id+"F0.wireOp",EDGE,"E5.3.0.0"),sQuery(id+"F0.wireOp",EDGE,"E5.3.1.0"),sQuery(id+"F0.wireOp",EDGE,"E5.3.2.0"),sQuery(id+"F0.wireOp",EDGE,"E5.3.3.0"),sQuery(id+"F0.wireOp",EDGE,"E5.3.4.0"),sQuery(id+"F0.wireOp",EDGE,"E5.3.5.0"),sQuery(id+"F0.wireOp",EDGE,"E5.4.0.0"),sQuery(id+"F0.wireOp",EDGE,"E5.4.1.0"),sQuery(id+"F0.wireOp",EDGE,"E5.4.2.0"),sQuery(id+"F0.wireOp",EDGE,"E5.4.3.0"),sQuery(id+"F0.wireOp",EDGE,"E5.4.4.0"),sQuery(id+"F0.wireOp",EDGE,"E5.4.5.0"),sQuery(id+"F0.wireOp",EDGE,"E5.5.0.0"),sQuery(id+"F0.wireOp",EDGE,"E5.5.1.0"),sQuery(id+"F0.wireOp",EDGE,"E5.5.2.0"),sQuery(id+"F0.wireOp",EDGE,"E5.5.3.0"),sQuery(id+"F0.wireOp",EDGE,"E5.5.4.0"),sQuery(id+"F0.wireOp",EDGE,"E5.5.5.0"),sQuery(id+"F0.wireOp",EDGE,"E5.6.0.0"),sQuery(id+"F0.wireOp",EDGE,"E5.6.1.0"),sQuery(id+"F0.wireOp",EDGE,"E5.6.2.0"),sQuery(id+"F0.wireOp",EDGE,"E5.6.3.0"),sQuery(id+"F0.wireOp",EDGE,"E5.6.4.0"),sQuery(id+"F0.wireOp",EDGE,"E5.6.5.0"),sQuery(id+"F0.wireOp",EDGE,"b43360bd-87d0-4ba4-b8e7-1d9b1ca2d7b7.0.7.0"),sQuery(id+"F0.wireOp",EDGE,"b43360bd-87d0-4ba4-b8e7-1d9b1ca2d7b7.0.7.1"),sQuery(id+"F0.wireOp",EDGE,"b43360bd-87d0-4ba4-b8e7-1d9b1ca2d7b7.0.7.2"),sQuery(id+"F0.wireOp",EDGE,"b43360bd-87d0-4ba4-b8e7-1d9b1ca2d7b7.0.7.3"),sQuery(id+"F0.wireOp",EDGE,"b43360bd-87d0-4ba4-b8e7-1d9b1ca2d7b7.0.7.4"),sQuery(id+"F0.wireOp",EDGE,"b43360bd-87d0-4ba4-b8e7-1d9b1ca2d7b7.0.7.5"),sQuery(id+"F0.wireOp",EDGE,"b43360bd-87d0-4ba4-b8e7-1d9b1ca2d7b7.0.8.0"),sQuery(id+"F0.wireOp",EDGE,"b43360bd-87d0-4ba4-b8e7-1d9b1ca2d7b7.0.8.1"),sQuery(id+"F0.wireOp",EDGE,"b43360bd-87d0-4ba4-b8e7-1d9b1ca2d7b7.0.8.2"),sQuery(id+"F0.wireOp",EDGE,"b43360bd-87d0-4ba4-b8e7-1d9b1ca2d7b7.0.8.3"),sQuery(id+"F0.wireOp",EDGE,"b43360bd-87d0-4ba4-b8e7-1d9b1ca2d7b7.0.8.4"),sQuery(id+"F0.wireOp",EDGE,"b43360bd-87d0-4ba4-b8e7-1d9b1ca2d7b7.0.8.5"),sQuery(id+"F0.wireOp",EDGE,"4d49d44f-d1c3-4a0c-bbbb-6a01bf94c153.0.9.0"),sQuery(id+"F0.wireOp",EDGE,"4d49d44f-d1c3-4a0c-bbbb-6a01bf94c153.0.9.1"),sQuery(id+"F0.wireOp",EDGE,"4d49d44f-d1c3-4a0c-bbbb-6a01bf94c153.0.9.2"),sQuery(id+"F0.wireOp",EDGE,"4d49d44f-d1c3-4a0c-bbbb-6a01bf94c153.0.9.3"),sQuery(id+"F0.wireOp",EDGE,"4d49d44f-d1c3-4a0c-bbbb-6a01bf94c153.0.9.4"),sQuery(id+"F0.wireOp",EDGE,"4d49d44f-d1c3-4a0c-bbbb-6a01bf94c153.0.9.5"),subQ3,subQ2,subQ1,subQ0,sQuery(id+"F0.wireOp",EDGE,"ce14f02e-7be2-4b20-84b1-1cf9d0b90355.0.0.6"),sQuery(id+"F0.wireOp",EDGE,"ce14f02e-7be2-4b20-84b1-1cf9d0b90355.0.0.7"),sQuery(id+"F0.wireOp",EDGE,"ce14f02e-7be2-4b20-84b1-1cf9d0b90355.0.1.6"),sQuery(id+"F0.wireOp",EDGE,"ce14f02e-7be2-4b20-84b1-1cf9d0b90355.0.1.7"),sQuery(id+"F0.wireOp",EDGE,"ce14f02e-7be2-4b20-84b1-1cf9d0b90355.0.2.6"),sQuery(id+"F0.wireOp",EDGE,"ce14f02e-7be2-4b20-84b1-1cf9d0b90355.0.2.7"),sQuery(id+"F0.wireOp",EDGE,"ce14f02e-7be2-4b20-84b1-1cf9d0b90355.0.3.6"),sQuery(id+"F0.wireOp",EDGE,"ce14f02e-7be2-4b20-84b1-1cf9d0b90355.0.3.7"),sQuery(id+"F0.wireOp",EDGE,"ce14f02e-7be2-4b20-84b1-1cf9d0b90355.0.4.6"),sQuery(id+"F0.wireOp",EDGE,"ce14f02e-7be2-4b20-84b1-1cf9d0b90355.0.4.7"),sQuery(id+"F0.wireOp",EDGE,"ce14f02e-7be2-4b20-84b1-1cf9d0b90355.0.5.6"),sQuery(id+"F0.wireOp",EDGE,"ce14f02e-7be2-4b20-84b1-1cf9d0b90355.0.5.7"),sQuery(id+"F0.wireOp",EDGE,"ce14f02e-7be2-4b20-84b1-1cf9d0b90355.0.6.6"),sQuery(id+"F0.wireOp",EDGE,"ce14f02e-7be2-4b20-84b1-1cf9d0b90355.0.6.7"),sQuery(id+"F0.wireOp",EDGE,"ce14f02e-7be2-4b20-84b1-1cf9d0b90355.0.7.6"),sQuery(id+"F0.wireOp",EDGE,"ce14f02e-7be2-4b20-84b1-1cf9d0b90355.0.7.7"),sQuery(id+"F0.wireOp",EDGE,"ce14f02e-7be2-4b20-84b1-1cf9d0b90355.0.8.6"),sQuery(id+"F0.wireOp",EDGE,"ce14f02e-7be2-4b20-84b1-1cf9d0b90355.0.8.7"),sQuery(id+"F0.wireOp",EDGE,"ce14f02e-7be2-4b20-84b1-1cf9d0b90355.0.9.6"),sQuery(id+"F0.wireOp",EDGE,"ce14f02e-7be2-4b20-84b1-1cf9d0b90355.0.9.7"),sQuery(id+"F0.wireOp",EDGE,"E17"),sQuery(id+"F0.wireOp",EDGE,"E18.0.1.0"),sQuery(id+"F0.wireOp",EDGE,"E18.0.2.0"),sQuery(id+"F0.wireOp",EDGE,"E18.0.3.0"),sQuery(id+"F0.wireOp",EDGE,"E18.0.4.0"),sQuery(id+"F0.wireOp",EDGE,"E18.0.5.0"),sQuery(id+"F0.wireOp",EDGE,"E18.0.6.0"),sQuery(id+"F0.wireOp",EDGE,"E18.1.0.0"),sQuery(id+"F0.wireOp",EDGE,"E18.1.1.0"),sQuery(id+"F0.wireOp",EDGE,"E18.1.2.0"),sQuery(id+"F0.wireOp",EDGE,"E18.1.3.0"),sQuery(id+"F0.wireOp",EDGE,"E18.1.4.0"),sQuery(id+"F0.wireOp",EDGE,"E18.1.5.0"),sQuery(id+"F0.wireOp",EDGE,"E18.1.6.0"),sQuery(id+"F0.wireOp",EDGE,"E18.2.0.0"),sQuery(id+"F0.wireOp",EDGE,"E18.2.1.0"),sQuery(id+"F0.wireOp",EDGE,"E18.2.2.0"),sQuery(id+"F0.wireOp",EDGE,"E18.2.3.0"),sQuery(id+"F0.wireOp",EDGE,"E18.2.4.0"),sQuery(id+"F0.wireOp",EDGE,"E18.2.5.0"),sQuery(id+"F0.wireOp",EDGE,"E18.2.6.0"),sQuery(id+"F0.wireOp",EDGE,"E18.3.0.0"),sQuery(id+"F0.wireOp",EDGE,"E18.3.1.0"),sQuery(id+"F0.wireOp",EDGE,"E18.3.2.0"),sQuery(id+"F0.wireOp",EDGE,"E18.3.3.0"),sQuery(id+"F0.wireOp",EDGE,"E18.3.4.0"),sQuery(id+"F0.wireOp",EDGE,"E18.3.5.0"),sQuery(id+"F0.wireOp",EDGE,"E18.3.6.0"),sQuery(id+"F0.wireOp",EDGE,"E18.4.0.0"),sQuery(id+"F0.wireOp",EDGE,"E18.4.1.0"),sQuery(id+"F0.wireOp",EDGE,"E18.4.2.0"),sQuery(id+"F0.wireOp",EDGE,"E18.4.3.0"),sQuery(id+"F0.wireOp",EDGE,"E18.4.4.0"),sQuery(id+"F0.wireOp",EDGE,"E18.4.5.0"),sQuery(id+"F0.wireOp",EDGE,"E18.4.6.0"),sQuery(id+"F0.wireOp",EDGE,"E18.5.0.0"),sQuery(id+"F0.wireOp",EDGE,"E18.5.1.0"),sQuery(id+"F0.wireOp",EDGE,"E18.5.2.0"),sQuery(id+"F0.wireOp",EDGE,"E18.5.3.0"),sQuery(id+"F0.wireOp",EDGE,"E18.5.4.0"),sQuery(id+"F0.wireOp",EDGE,"E18.5.5.0"),sQuery(id+"F0.wireOp",EDGE,"E18.5.6.0"),sQuery(id+"F0.wireOp",EDGE,"E18.6.0.0"),sQuery(id+"F0.wireOp",EDGE,"E18.6.1.0"),sQuery(id+"F0.wireOp",EDGE,"E18.6.2.0"),sQuery(id+"F0.wireOp",EDGE,"E18.6.3.0"),sQuery(id+"F0.wireOp",EDGE,"E18.6.4.0"),sQuery(id+"F0.wireOp",EDGE,"E18.6.5.0"),sQuery(id+"F0.wireOp",EDGE,"E18.6.6.0"),sQuery(id+"F0.wireOp",EDGE,"E18.7.0.0"),sQuery(id+"F0.wireOp",EDGE,"E18.7.1.0"),sQuery(id+"F0.wireOp",EDGE,"E18.7.2.0"),sQuery(id+"F0.wireOp",EDGE,"E18.7.3.0"),sQuery(id+"F0.wireOp",EDGE,"E18.7.4.0"),sQuery(id+"F0.wireOp",EDGE,"E18.7.5.0"),sQuery(id+"F0.wireOp",EDGE,"E18.7.6.0"),sQuery(id+"F0.wireOp",EDGE,"E18.8.0.0"),sQuery(id+"F0.wireOp",EDGE,"E18.8.1.0"),sQuery(id+"F0.wireOp",EDGE,"E18.8.2.0"),sQuery(id+"F0.wireOp",EDGE,"E18.8.3.0"),sQuery(id+"F0.wireOp",EDGE,"E18.8.4.0"),sQuery(id+"F0.wireOp",EDGE,"E18.8.5.0"),sQuery(id+"F0.wireOp",EDGE,"E18.8.6.0"),sQuery(id+"F0.wireOp",EDGE,"E18.9.0.0"),sQuery(id+"F0.wireOp",EDGE,"E18.9.1.0"),sQuery(id+"F0.wireOp",EDGE,"E18.9.2.0"),sQuery(id+"F0.wireOp",EDGE,"E18.9.3.0"),sQuery(id+"F0.wireOp",EDGE,"E18.9.4.0"),sQuery(id+"F0.wireOp",EDGE,"E18.9.5.0"),sQuery(id+"F0.wireOp",EDGE,"E18.9.6.0"),sQuery(id+"F0.wireOp",EDGE,"0ecf2793-63ef-4b24-9386-6ba147f8df1b.0.0.7"),sQuery(id+"F0.wireOp",EDGE,"0ecf2793-63ef-4b24-9386-6ba147f8df1b.0.1.7"),sQuery(id+"F0.wireOp",EDGE,"0ecf2793-63ef-4b24-9386-6ba147f8df1b.0.2.7"),sQuery(id+"F0.wireOp",EDGE,"0ecf2793-63ef-4b24-9386-6ba147f8df1b.0.3.7"),sQuery(id+"F0.wireOp",EDGE,"0ecf2793-63ef-4b24-9386-6ba147f8df1b.0.4.7"),sQuery(id+"F0.wireOp",EDGE,"0ecf2793-63ef-4b24-9386-6ba147f8df1b.0.5.7"),sQuery(id+"F0.wireOp",EDGE,"0ecf2793-63ef-4b24-9386-6ba147f8df1b.0.6.7"),sQuery(id+"F0.wireOp",EDGE,"0ecf2793-63ef-4b24-9386-6ba147f8df1b.0.7.7"),sQuery(id+"F0.wireOp",EDGE,"0ecf2793-63ef-4b24-9386-6ba147f8df1b.0.8.7"),sQuery(id+"F0.wireOp",EDGE,"0ecf2793-63ef-4b24-9386-6ba147f8df1b.0.9.7")])],"isStart":true}),makeQuery(id+"F4.opExtrude","CAP_FACE",FACE,{"disambiguationData":[OSD([subQ3,subQ2,subQ1,subQ0,sQuery(id+"F3.wireOp",EDGE,"E26.0"),sQuery(id+"F3.wireOp",EDGE,"E26.1"),sQuery(id+"F3.wireOp",EDGE,"E26.2"),sQuery(id+"F3.wireOp",EDGE,"E26.3")])],"isStart":true})]});}
            extrude(context, id + "F5", {"entities" : qUnion([Q0]), "depth" : 1 * mm});
        }
    });
